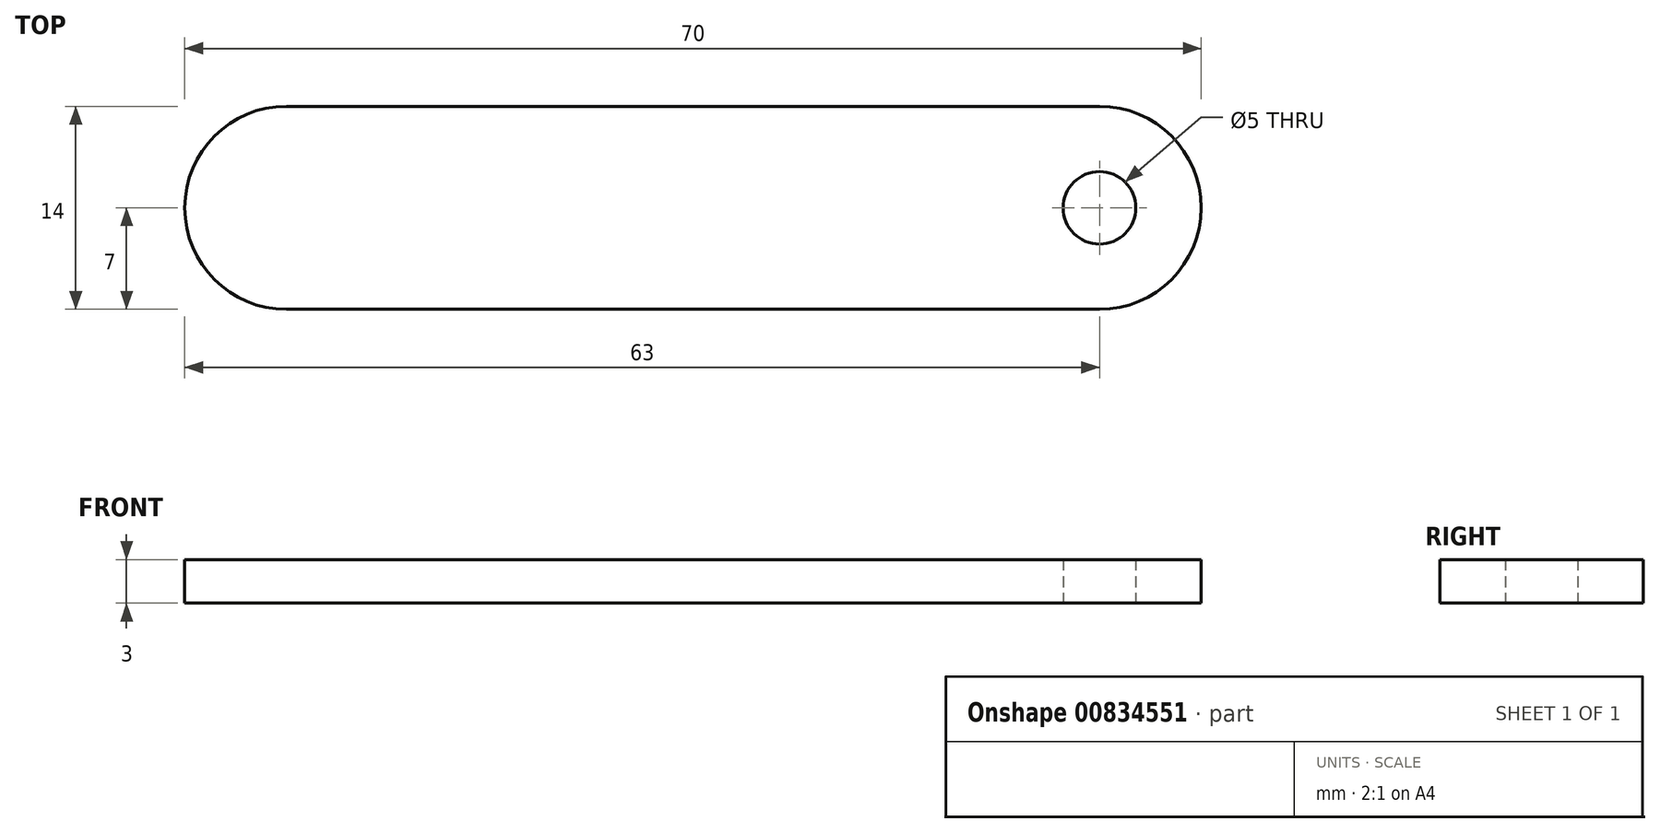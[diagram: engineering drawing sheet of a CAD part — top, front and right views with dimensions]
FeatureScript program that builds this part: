
annotation { "Feature Type Name" : "Feature", "Feature Type Description" : "" }
export const myFeature = defineFeature(function(context is Context, id is Id, definition is map)
    precondition{}
    {
        {
            var Q0;
            Q0=qCreatedBy(makeId("Top.planeOp"),FACE);
            var sketch = newSketch(context, id + "F0", { "sketchPlane" : qUnion([Q0])});
            skLineSegment(sketch, "E0.bottom", {"start": v(35, 7) * mm, "end": v(-35, 7) * mm});
            skLineSegment(sketch, "E0.top", {"start": v(35, -7) * mm, "end": v(-35, -7) * mm});
            skLineSegment(sketch, "E0.left", {"start": v(35, 7) * mm, "end": v(35, -7) * mm});
            skLineSegment(sketch, "E0.right", {"start": v(-35, 7) * mm, "end": v(-35, -7) * mm});
            skPoint(sketch, "E0.middle", {"position": v(0, 0) * mm});
            skCircle(sketch, "E1", {"center": v(28, 0) * mm, "radius": 2.5 * mm});
            skSolve(sketch);
        }
        {
            var Q0;
            Q0=makeQuery(id+"F0.imprint","IMPRINT",FACE,{"disambiguationData":[TD([[makeQuery(id+"F0.imprint","IMPRINT",EDGE,{"derivedFrom":sQuery(id+"F0.wireOp",EDGE,"E0.bottom")}),1.0]])]});
            extrude(context, id + "F1", {"entities" : qUnion([Q0]), "depth" : 3 * mm, "offsetDistance" : 25 * mm});
        }
        {
            var Q0;
            Q0=makeQuery(id+"F1.opExtrude","SWEPT_EDGE",EDGE,{"disambiguationData":[OSD([sQuery(id+"F0.wireOp",EDGE,"E0.bottom"),sQuery(id+"F0.wireOp",EDGE,"E0.left")])]});
            var Q1;
            Q1=makeQuery(id+"F1.opExtrude","SWEPT_EDGE",EDGE,{"disambiguationData":[OSD([sQuery(id+"F0.wireOp",EDGE,"E0.top"),sQuery(id+"F0.wireOp",EDGE,"E0.left")])]});
            var Q2;
            Q2=makeQuery(id+"F1.opExtrude","SWEPT_EDGE",EDGE,{"disambiguationData":[OSD([sQuery(id+"F0.wireOp",EDGE,"E0.top"),sQuery(id+"F0.wireOp",EDGE,"E0.right")])]});
            var Q3;
            Q3=makeQuery(id+"F1.opExtrude","SWEPT_EDGE",EDGE,{"disambiguationData":[OSD([sQuery(id+"F0.wireOp",EDGE,"E0.bottom"),sQuery(id+"F0.wireOp",EDGE,"E0.right")])]});
            fillet(context, id + "F2", {"entities" : qUnion([Q0, Q1, Q2, Q3]), "radius" : 7 * mm, "tangentPropagation" : true, "allowEdgeOverflow" : false});
        }
    });
